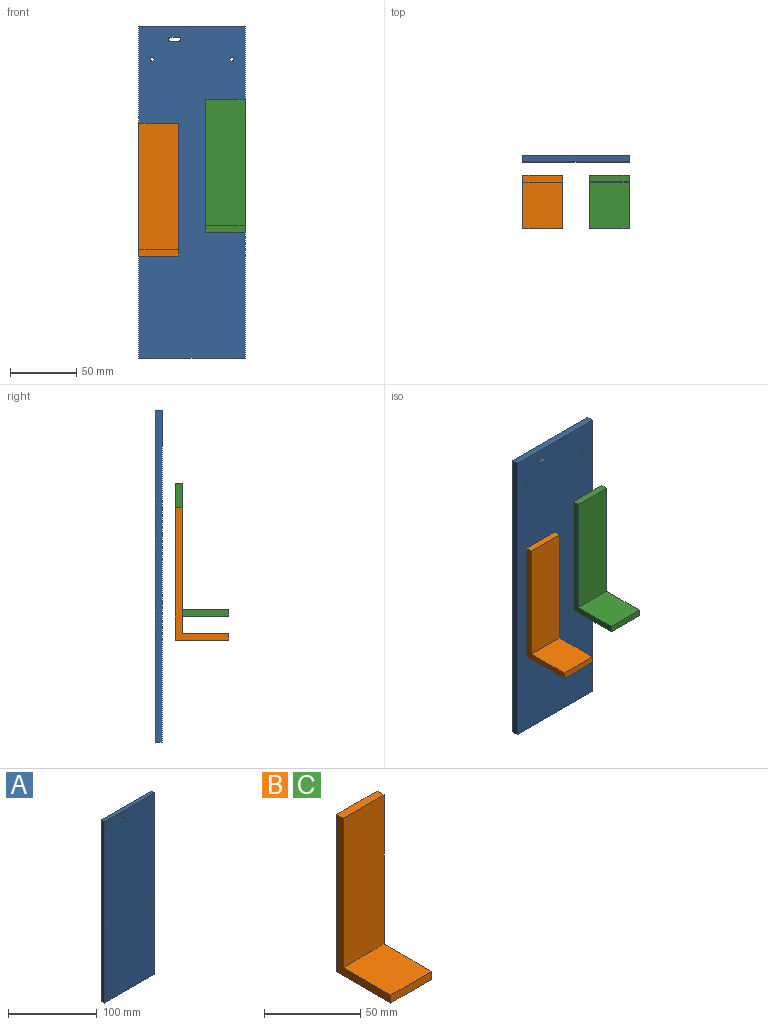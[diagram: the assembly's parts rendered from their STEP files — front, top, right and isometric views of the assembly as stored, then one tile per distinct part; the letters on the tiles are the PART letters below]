
ASSEMBLY  parts=3 mates=5
PART A: 14 faces, bbox 80x5x250 mm
  f0: plane 80x5mm, normal (0,0,1), area 400mm2, adj f1,f11,f12,f13
  f1: plane 250x5mm, normal (-1,0,0), area 1250mm2, adj f0,f2,f12,f13
  f2: plane 80x5mm, normal (0,0,-1), area 400mm2, adj f1,f11,f12,f13
  f3: plane 6x5mm, normal (0,0,-1), area 30mm2, adj f4,f10,f12,f13
  f4: cylinder r=1.5mm len=5mm, axis (0,1,0), area 23.6mm2, adj f3,f5,f12,f13
  f5: plane 6x5mm, normal (0,0,1), area 30mm2, adj f4,f10,f12,f13
  f6: cylinder r=1.5mm len=5mm, axis (0,1,0), area 47.1mm2, adj f12,f13
  f7: cylinder r=1.5mm len=5mm, axis (0,1,0), area 47.1mm2, adj f12,f13
  f8: cylinder r=1.5mm len=5mm, axis (0,1,0), area 47.1mm2, adj f12,f13
  f9: cylinder r=1.5mm len=5mm, axis (0,1,0), area 47.1mm2, adj f12,f13
  f10: cylinder r=1.5mm len=5mm, axis (0,1,0), area 23.6mm2, adj f3,f5,f12,f13
  f11: plane 250x5mm, normal (1,0,0), area 1250mm2, adj f0,f2,f12,f13
  f12: plane 250x80mm, normal (0,-1,0), area 19946.7mm2, adj f0,f1,f2,f3,f4,f5,f6,f7
  f13: plane 250x80mm, normal (0,1,0), area 19946.7mm2, adj f0,f1,f2,f3,f4,f5,f6,f7
PART B: 8 faces, bbox 30x40x100 mm
  f0: plane 40x30mm, normal (0,0,-1), area 1200mm2, adj f1,f5,f6,f7
  f1: plane 100x30mm, normal (0,1,0), area 3000mm2, adj f0,f2,f6,f7
  f2: plane 30x5mm, normal (0,0,1), area 150mm2, adj f1,f3,f6,f7
  f3: plane 95x30mm, normal (0,-1,0), area 2850mm2, adj f2,f4,f6,f7
  f4: plane 35x30mm, normal (0,0,1), area 1050mm2, adj f3,f5,f6,f7
  f5: plane 30x5mm, normal (0,-1,0), area 150mm2, adj f0,f4,f6,f7
  f6: plane 100x40mm, normal (1,0,0), area 675mm2, adj f0,f1,f2,f3,f4,f5
  f7: plane 100x40mm, normal (-1,0,0), area 675mm2, adj f0,f1,f2,f3,f4,f5
PART C: same geometry as B
PLACE A at identity fixed
PLACE B t=(-25,-15,-48.3)mm
PLACE C t=(25,-15,-30.28)mm
MATE parallel A.f11 <-> C.f6  axis (1,0,0) through (40,-2.5,0)mm
MATE planar B.f7 <-> A.f1  axis (-1,0,0) through (-40,-15,-48.3)mm
MATE parallel C.f0 <-> A.f2  axis (0,0,-1) through (25,-35,-30.28)mm
MATE parallel C.f1 <-> A.f12  axis (0,1,0) through (25,-15,19.72)mm
MATE planar C.f1 <-> B.f1  axis (0,1,0) through (25,-15,19.72)mm
